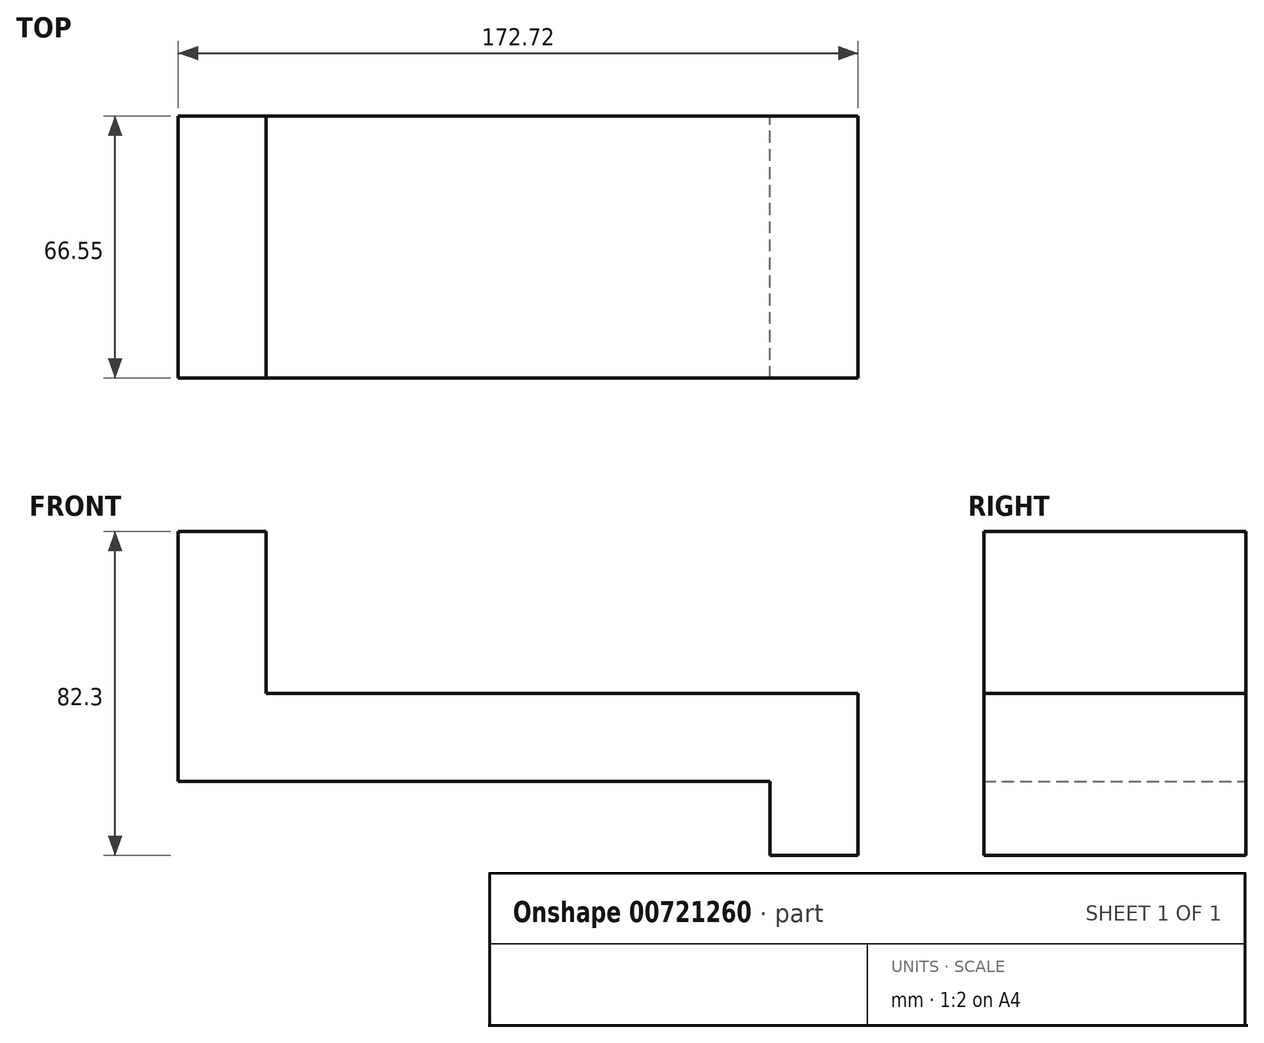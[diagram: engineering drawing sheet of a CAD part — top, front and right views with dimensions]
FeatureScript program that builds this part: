
annotation { "Feature Type Name" : "Feature", "Feature Type Description" : "" }
export const myFeature = defineFeature(function(context is Context, id is Id, definition is map)
    precondition{}
    {
        {
            var Q0;
            Q0=qCreatedBy(makeId("Front.planeOp"),FACE);
            var sketch = newSketch(context, id + "F0", { "sketchPlane" : qUnion([Q0])});
            skLineSegment(sketch, "E0", {"start": v(-74.62, 13.88) * mm, "end": v(75.75, 13.88) * mm});
            skLineSegment(sketch, "E1", {"start": v(75.75, 13.88) * mm, "end": v(75.75, -27.27) * mm});
            skLineSegment(sketch, "E2", {"start": v(75.75, -27.27) * mm, "end": v(53.4, -27.27) * mm});
            skLineSegment(sketch, "E3", {"start": v(-74.62, 13.88) * mm, "end": v(-74.62, 55.03) * mm});
            skLineSegment(sketch, "E4", {"start": v(-74.62, 55.03) * mm, "end": v(-96.97, 55.03) * mm});
            skLineSegment(sketch, "E5", {"start": v(-96.97, 55.03) * mm, "end": v(-96.97, -8.47) * mm});
            skLineSegment(sketch, "E6", {"start": v(-96.97, -8.47) * mm, "end": v(53.4, -8.47) * mm});
            skLineSegment(sketch, "E7", {"start": v(53.4, -8.47) * mm, "end": v(53.4, -27.27) * mm});
            skSolve(sketch);
        }
        {
            var Q0;
            Q0=makeQuery(id+"F0.imprint","IMPRINT",FACE,{"disambiguationData":[TD([[makeQuery(id+"F0.imprint","IMPRINT",EDGE,{"derivedFrom":sQuery(id+"F0.wireOp",EDGE,"E0")}),-1.0]])]});
            extrude(context, id + "F1", {"entities" : qUnion([Q0]), "depth" : 66.55 * mm, "offsetDistance" : 25.4 * mm});
        }
    });
